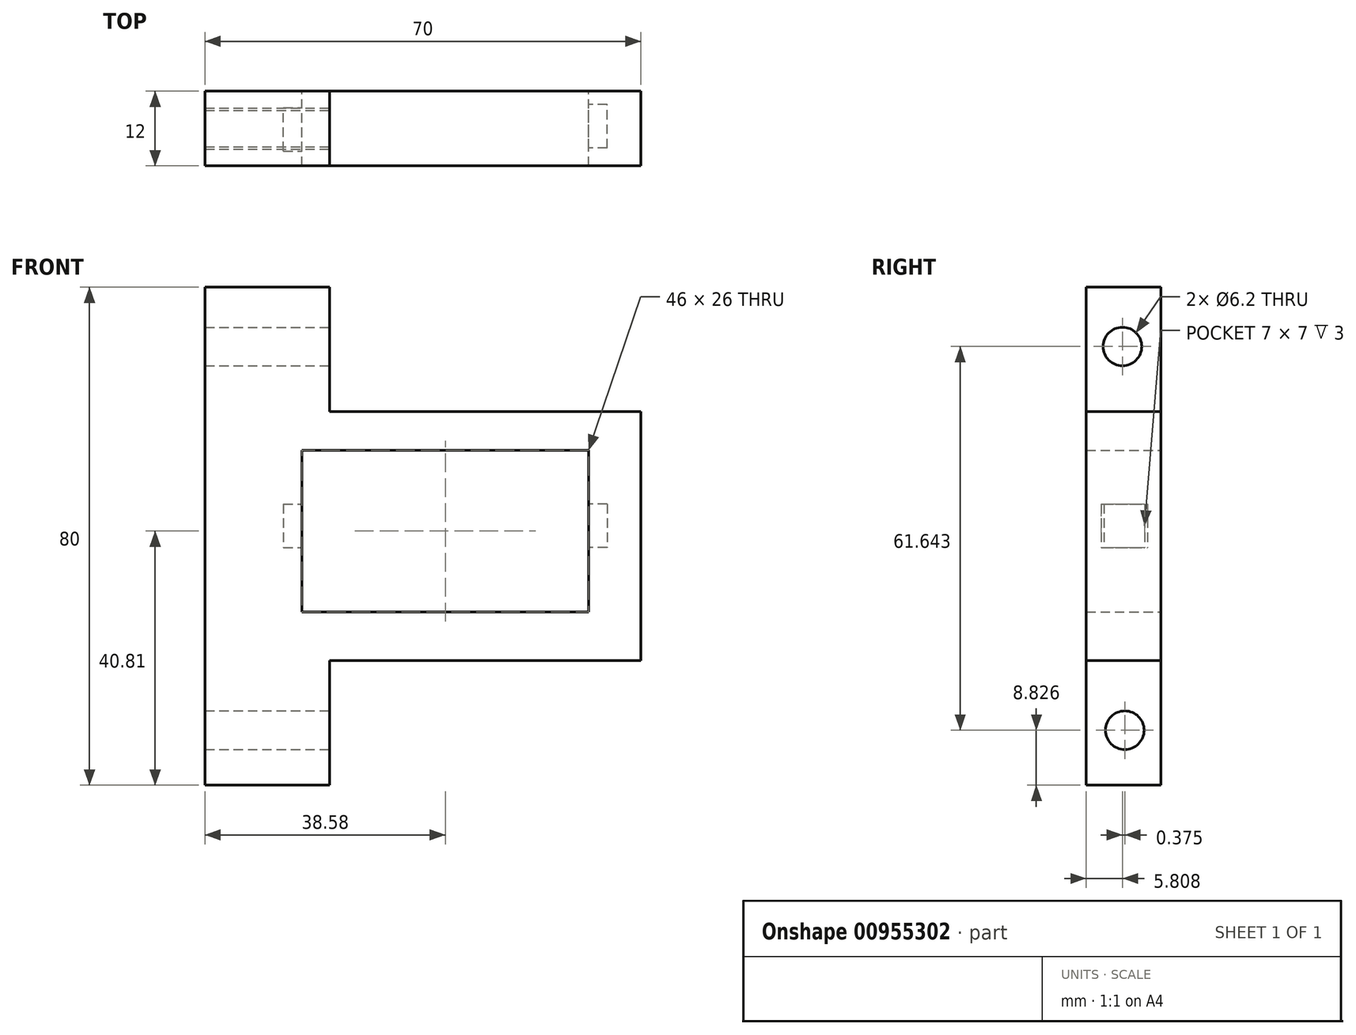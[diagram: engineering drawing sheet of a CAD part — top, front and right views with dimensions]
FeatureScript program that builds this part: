
annotation { "Feature Type Name" : "Feature", "Feature Type Description" : "" }
export const myFeature = defineFeature(function(context is Context, id is Id, definition is map)
    precondition{}
    {
        {
            var Q0;
            Q0=qCreatedBy(makeId("Front.planeOp"),FACE);
            var sketch = newSketch(context, id + "F0", { "sketchPlane" : qUnion([Q0])});
            skLineSegment(sketch, "E0.bottom", {"start": v(0, 0) * mm, "end": v(46, 0) * mm});
            skLineSegment(sketch, "E0.top", {"start": v(0, 26) * mm, "end": v(46, 26) * mm});
            skLineSegment(sketch, "E0.left", {"start": v(0, 0) * mm, "end": v(0, 26) * mm});
            skLineSegment(sketch, "E0.right", {"start": v(46, 0) * mm, "end": v(46, 26) * mm});
            skLineSegment(sketch, "E1", {"start": v(4.42, -7.81) * mm, "end": v(54.42, -7.81) * mm});
            skLineSegment(sketch, "E2", {"start": v(54.42, -7.81) * mm, "end": v(54.42, 32.19) * mm});
            skLineSegment(sketch, "E3", {"start": v(54.42, 32.19) * mm, "end": v(4.42, 32.19) * mm});
            skLineSegment(sketch, "E4", {"start": v(4.42, 32.19) * mm, "end": v(4.42, 52.19) * mm});
            skLineSegment(sketch, "E5", {"start": v(4.42, 52.19) * mm, "end": v(-15.58, 52.19) * mm});
            skLineSegment(sketch, "E6", {"start": v(4.42, -7.81) * mm, "end": v(4.42, -27.81) * mm});
            skLineSegment(sketch, "E7", {"start": v(4.42, -27.81) * mm, "end": v(-15.58, -27.81) * mm});
            skLineSegment(sketch, "E8", {"start": v(-15.58, 52.19) * mm, "end": v(-15.58, -27.81) * mm});
            skSolve(sketch);
        }
        {
            var Q0;
            Q0=qCreatedBy(makeId("Right.planeOp"),FACE);
            cPlane(context, id + "F1", {"entities" : qUnion([Q0]), "cplaneType" : CPlaneType.OFFSET, "offset" : 25 * mm, "width" : 150 * mm, "height" : 150 * mm});
        }
        {
            var Q0;
            Q0 = qSketchRegion(id + "F0", true);
            extrude(context, id + "F2", {"entities" : qUnion([Q0]), "depth" : 12 * mm, "offsetDistance" : 25 * mm});
        }
        {
            var Q0;
            Q0=qCreatedBy(id+"F1.planeOp",FACE);
            var sketch = newSketch(context, id + "F3", { "sketchPlane" : qUnion([Q0])});
            skCircle(sketch, "E9", {"center": v(-6.2, 42.66) * mm, "radius": 3 * mm});
            skCircle(sketch, "E10", {"center": v(-5.82, -18.98) * mm, "radius": 3 * mm});
            skSolve(sketch);
        }
        {
            var Q0;
            Q0=sQuery(id+"F3.wireOp",VERTEX,"E9.center");
            var Q1;
            Q1=makeQuery(id+"F2.opExtrude","SWEPT_BODY",BODY,{"disambiguationData":[OSD([sQuery(id+"F0.wireOp",EDGE,"E0.bottom"),sQuery(id+"F0.wireOp",EDGE,"E0.top"),sQuery(id+"F0.wireOp",EDGE,"E0.left"),sQuery(id+"F0.wireOp",EDGE,"E0.right"),sQuery(id+"F0.wireOp",EDGE,"E1"),sQuery(id+"F0.wireOp",EDGE,"E2"),sQuery(id+"F0.wireOp",EDGE,"E3"),sQuery(id+"F0.wireOp",EDGE,"E4"),sQuery(id+"F0.wireOp",EDGE,"E5"),sQuery(id+"F0.wireOp",EDGE,"E6"),sQuery(id+"F0.wireOp",EDGE,"E7"),sQuery(id+"F0.wireOp",EDGE,"E8")])]});
            hole(context, id + "F4", {"style" : HoleStyle.SIMPLE, "endStyle" : HoleEndStyle.THROUGH, "holeDiameter" : 6.2 * mm, "majorDiameter" : 5 * mm, "isTappedThrough" : true, "tappedDepth" : 12 * mm, "tapClearance" : 3, "locations" : qUnion([Q0]), "scope" : qUnion([Q1])});
        }
        {
            var Q0;
            Q0=sQuery(id+"F3.wireOp",VERTEX,"E10.center");
            var Q1;
            Q1=makeQuery(id+"F2.opExtrude","SWEPT_BODY",BODY,{"disambiguationData":[OSD([sQuery(id+"F0.wireOp",EDGE,"E0.bottom"),sQuery(id+"F0.wireOp",EDGE,"E0.top"),sQuery(id+"F0.wireOp",EDGE,"E0.left"),sQuery(id+"F0.wireOp",EDGE,"E0.right"),sQuery(id+"F0.wireOp",EDGE,"E1"),sQuery(id+"F0.wireOp",EDGE,"E2"),sQuery(id+"F0.wireOp",EDGE,"E3"),sQuery(id+"F0.wireOp",EDGE,"E4"),sQuery(id+"F0.wireOp",EDGE,"E5"),sQuery(id+"F0.wireOp",EDGE,"E6"),sQuery(id+"F0.wireOp",EDGE,"E7"),sQuery(id+"F0.wireOp",EDGE,"E8")])]});
            hole(context, id + "F5", {"style" : HoleStyle.SIMPLE, "endStyle" : HoleEndStyle.THROUGH, "holeDiameter" : 6.2 * mm, "majorDiameter" : 5 * mm, "isTappedThrough" : true, "tappedDepth" : 12 * mm, "tapClearance" : 3, "locations" : qUnion([Q0]), "scope" : qUnion([Q1])});
        }
        {
            var Q0;
            Q0=qCreatedBy(makeId("Right.planeOp"),FACE);
            cPlane(context, id + "F6", {"entities" : qUnion([Q0]), "cplaneType" : CPlaneType.OFFSET, "offset" : 46 * mm, "width" : 150 * mm, "height" : 150 * mm});
        }
        {
            var Q0;
            Q0=qCreatedBy(makeId("Right.planeOp"),FACE);
            var sketch = newSketch(context, id + "F7", { "sketchPlane" : qUnion([Q0])});
            skLineSegment(sketch, "E11.bottom", {"start": v(-9.63, 17.35) * mm, "end": v(-2.63, 17.35) * mm});
            skLineSegment(sketch, "E11.top", {"start": v(-9.63, 10.35) * mm, "end": v(-2.63, 10.35) * mm});
            skLineSegment(sketch, "E11.left", {"start": v(-9.63, 17.35) * mm, "end": v(-9.63, 10.35) * mm});
            skLineSegment(sketch, "E11.right", {"start": v(-2.63, 17.35) * mm, "end": v(-2.63, 10.35) * mm});
            skSolve(sketch);
        }
        {
            var Q0;
            Q0 = qSketchRegion(id + "F7", true);
            extrude(context, id + "F8", {"entities" : qUnion([Q0]), "operationType" : NewBodyOperationType.REMOVE, "oppositeDirection" : true, "depth" : 3 * mm, "offsetDistance" : 25 * mm});
        }
        {
            var Q0;
            Q0=qCreatedBy(id+"F6.planeOp",FACE);
            var sketch = newSketch(context, id + "F9", { "sketchPlane" : qUnion([Q0])});
            skLineSegment(sketch, "E12.bottom", {"start": v(-9.16, 17.35) * mm, "end": v(-2.16, 17.35) * mm});
            skLineSegment(sketch, "E12.top", {"start": v(-9.16, 10.35) * mm, "end": v(-2.16, 10.35) * mm});
            skLineSegment(sketch, "E12.left", {"start": v(-9.16, 17.35) * mm, "end": v(-9.16, 10.35) * mm});
            skLineSegment(sketch, "E12.right", {"start": v(-2.16, 17.35) * mm, "end": v(-2.16, 10.35) * mm});
            skSolve(sketch);
        }
        {
            var Q0;
            Q0 = qSketchRegion(id + "F9", true);
            extrude(context, id + "F10", {"entities" : qUnion([Q0]), "operationType" : NewBodyOperationType.REMOVE, "depth" : 3 * mm, "offsetDistance" : 25 * mm});
        }
    });
